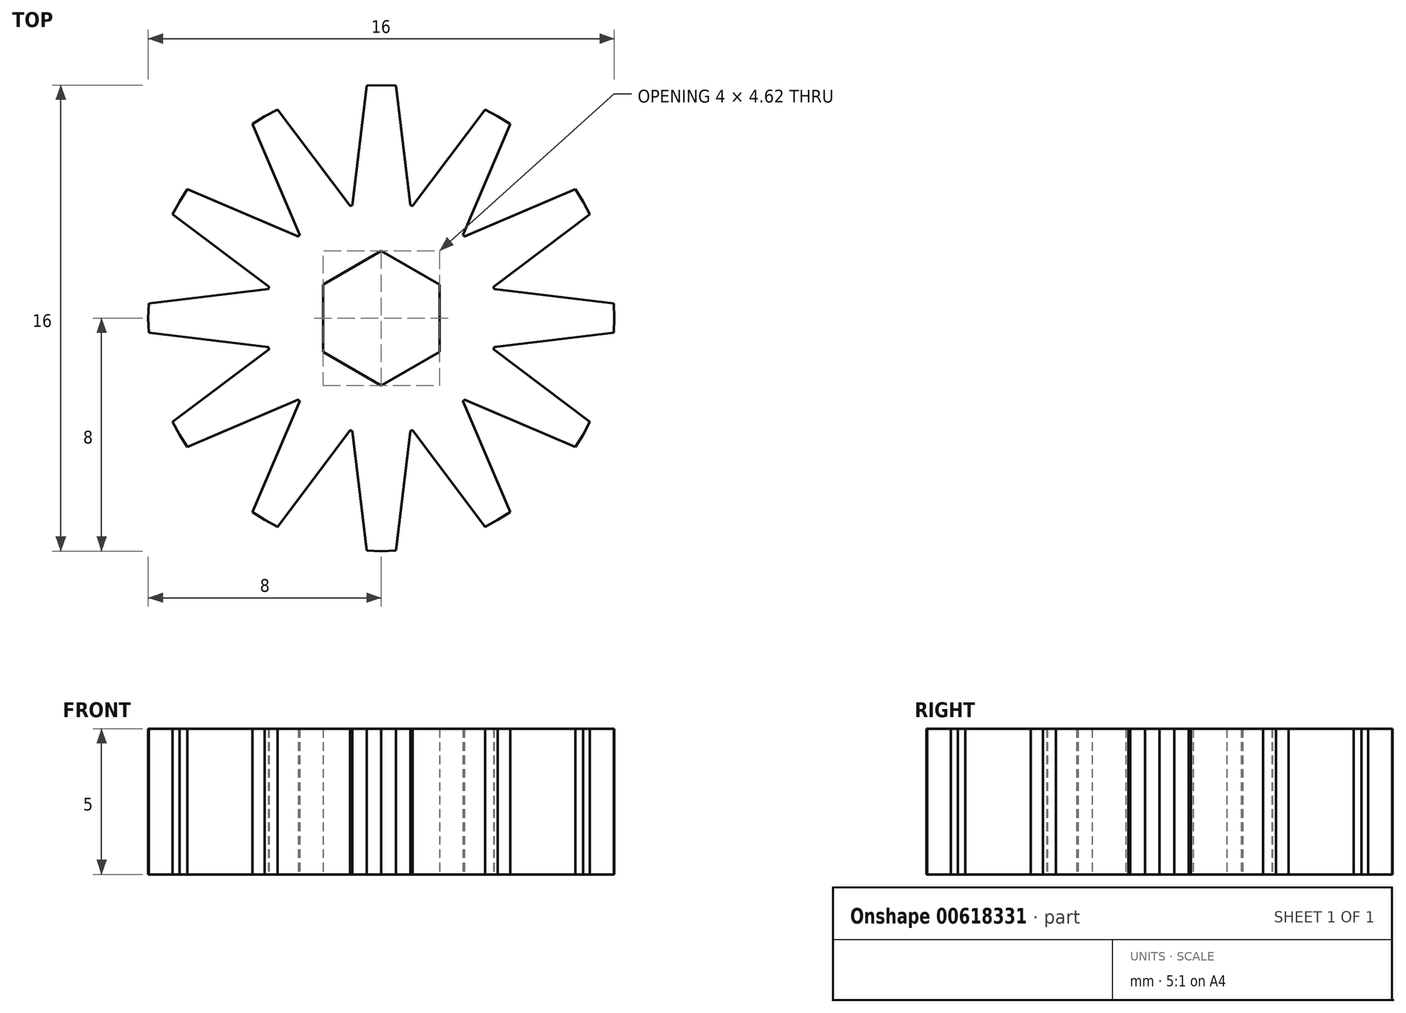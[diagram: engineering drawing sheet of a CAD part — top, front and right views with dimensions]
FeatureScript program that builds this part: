
annotation { "Feature Type Name" : "Feature", "Feature Type Description" : "" }
export const myFeature = defineFeature(function(context is Context, id is Id, definition is map)
    precondition{}
    {
        {
            var Q0;
            Q0=qCreatedBy(makeId("Top.planeOp"),FACE);
            var sketch = newSketch(context, id + "F0", { "sketchPlane" : qUnion([Q0])});
            skCircle(sketch, "E0", {"center": v(0, 0) * mm, "radius": 2 * mm});
            skCircle(sketch, "E1", {"center": v(0, 0) * mm, "radius": 8 * mm});
            skCircle(sketch, "E2.cCircle", {"center": v(0, 0) * mm, "radius": 2 * mm, "construction": true});
            skLineSegment(sketch, "E2.0", {"start": v(2, 1.15) * mm, "end": v(2, -1.15) * mm});
            skLineSegment(sketch, "E2.1", {"start": v(2, -1.15) * mm, "end": v(0, -2.3) * mm});
            skLineSegment(sketch, "E2.2", {"start": v(0, -2.3) * mm, "end": v(-2, -1.15) * mm});
            skLineSegment(sketch, "E2.3", {"start": v(-2, -1.15) * mm, "end": v(-2, 1.15) * mm});
            skLineSegment(sketch, "E2.4", {"start": v(-2, 1.15) * mm, "end": v(0, 2.3) * mm});
            skLineSegment(sketch, "E2.5", {"start": v(0, 2.3) * mm, "end": v(2, 1.15) * mm});
            skCircle(sketch, "E3", {"center": v(0, 0) * mm, "radius": 4 * mm});
            skLineSegment(sketch, "E4", {"start": v(0, 8) * mm, "end": v(-0.5, 7.98) * mm});
            skLineSegment(sketch, "E5", {"start": v(-0.5, 7.98) * mm, "end": v(-1, 3.87) * mm});
            skLineSegment(sketch, "E6.MirrorCS", {"start": v(0.5, 7.98) * mm, "end": v(1, 3.87) * mm});
            skLineSegment(sketch, "E7.MirrorCS", {"start": v(0, 8) * mm, "end": v(0.5, 7.98) * mm});
            skPoint(sketch, "E8.center", {"position": v(0, 2) * mm});
            skLineSegment(sketch, "E9.1.0", {"start": v(-4.42, 6.66) * mm, "end": v(-2.8, 2.85) * mm});
            skLineSegment(sketch, "E9.1.1", {"start": v(-4, 6.93) * mm, "end": v(-3.56, 7.16) * mm});
            skLineSegment(sketch, "E9.1.2", {"start": v(-4, 6.93) * mm, "end": v(-4.42, 6.66) * mm});
            skLineSegment(sketch, "E9.1.3", {"start": v(-3.56, 7.16) * mm, "end": v(-1.07, 3.85) * mm});
            skLineSegment(sketch, "E9.2.0", {"start": v(-7.16, 3.56) * mm, "end": v(-3.85, 1.07) * mm});
            skLineSegment(sketch, "E9.2.1", {"start": v(-6.93, 4) * mm, "end": v(-6.66, 4.42) * mm});
            skLineSegment(sketch, "E9.2.2", {"start": v(-6.93, 4) * mm, "end": v(-7.16, 3.56) * mm});
            skLineSegment(sketch, "E9.2.3", {"start": v(-6.66, 4.42) * mm, "end": v(-2.85, 2.8) * mm});
            skLineSegment(sketch, "E9.3.0", {"start": v(-7.98, -0.5) * mm, "end": v(-3.87, -1) * mm});
            skLineSegment(sketch, "E9.3.1", {"start": v(-8, 0) * mm, "end": v(-7.98, 0.5) * mm});
            skLineSegment(sketch, "E9.3.2", {"start": v(-8, 0) * mm, "end": v(-7.98, -0.5) * mm});
            skLineSegment(sketch, "E9.3.3", {"start": v(-7.98, 0.5) * mm, "end": v(-3.87, 1) * mm});
            skLineSegment(sketch, "E9.4.0", {"start": v(-6.66, -4.42) * mm, "end": v(-2.85, -2.8) * mm});
            skLineSegment(sketch, "E9.4.1", {"start": v(-6.93, -4) * mm, "end": v(-7.16, -3.56) * mm});
            skLineSegment(sketch, "E9.4.2", {"start": v(-6.93, -4) * mm, "end": v(-6.66, -4.42) * mm});
            skLineSegment(sketch, "E9.4.3", {"start": v(-7.16, -3.56) * mm, "end": v(-3.85, -1.07) * mm});
            skLineSegment(sketch, "E9.5.0", {"start": v(-3.56, -7.16) * mm, "end": v(-1.07, -3.85) * mm});
            skLineSegment(sketch, "E9.5.1", {"start": v(-4, -6.93) * mm, "end": v(-4.42, -6.66) * mm});
            skLineSegment(sketch, "E9.5.2", {"start": v(-4, -6.93) * mm, "end": v(-3.56, -7.16) * mm});
            skLineSegment(sketch, "E9.5.3", {"start": v(-4.42, -6.66) * mm, "end": v(-2.8, -2.85) * mm});
            skLineSegment(sketch, "E9.6.0", {"start": v(0.5, -7.98) * mm, "end": v(1, -3.87) * mm});
            skLineSegment(sketch, "E9.6.1", {"start": v(0, -8) * mm, "end": v(-0.5, -7.98) * mm});
            skLineSegment(sketch, "E9.6.2", {"start": v(0, -8) * mm, "end": v(0.5, -7.98) * mm});
            skLineSegment(sketch, "E9.6.3", {"start": v(-0.5, -7.98) * mm, "end": v(-1, -3.87) * mm});
            skLineSegment(sketch, "E9.7.0", {"start": v(4.42, -6.66) * mm, "end": v(2.8, -2.85) * mm});
            skLineSegment(sketch, "E9.7.1", {"start": v(4, -6.93) * mm, "end": v(3.56, -7.16) * mm});
            skLineSegment(sketch, "E9.7.2", {"start": v(4, -6.93) * mm, "end": v(4.42, -6.66) * mm});
            skLineSegment(sketch, "E9.7.3", {"start": v(3.56, -7.16) * mm, "end": v(1.07, -3.85) * mm});
            skLineSegment(sketch, "E9.8.0", {"start": v(7.16, -3.56) * mm, "end": v(3.85, -1.07) * mm});
            skLineSegment(sketch, "E9.8.1", {"start": v(6.93, -4) * mm, "end": v(6.66, -4.42) * mm});
            skLineSegment(sketch, "E9.8.2", {"start": v(6.93, -4) * mm, "end": v(7.16, -3.56) * mm});
            skLineSegment(sketch, "E9.8.3", {"start": v(6.66, -4.42) * mm, "end": v(2.85, -2.8) * mm});
            skLineSegment(sketch, "E9.9.0", {"start": v(7.98, 0.5) * mm, "end": v(3.87, 1) * mm});
            skLineSegment(sketch, "E9.9.1", {"start": v(8, 0) * mm, "end": v(7.98, -0.5) * mm});
            skLineSegment(sketch, "E9.9.2", {"start": v(8, 0) * mm, "end": v(7.98, 0.5) * mm});
            skLineSegment(sketch, "E9.9.3", {"start": v(7.98, -0.5) * mm, "end": v(3.87, -1) * mm});
            skLineSegment(sketch, "E9.10.0", {"start": v(6.66, 4.42) * mm, "end": v(2.85, 2.8) * mm});
            skLineSegment(sketch, "E9.10.1", {"start": v(6.93, 4) * mm, "end": v(7.16, 3.56) * mm});
            skLineSegment(sketch, "E9.10.2", {"start": v(6.93, 4) * mm, "end": v(6.66, 4.42) * mm});
            skLineSegment(sketch, "E9.10.3", {"start": v(7.16, 3.56) * mm, "end": v(3.85, 1.07) * mm});
            skLineSegment(sketch, "E9.11.0", {"start": v(3.56, 7.16) * mm, "end": v(1.07, 3.85) * mm});
            skLineSegment(sketch, "E9.11.1", {"start": v(4, 6.93) * mm, "end": v(4.42, 6.66) * mm});
            skLineSegment(sketch, "E9.11.2", {"start": v(4, 6.93) * mm, "end": v(3.56, 7.16) * mm});
            skLineSegment(sketch, "E9.11.3", {"start": v(4.42, 6.66) * mm, "end": v(2.8, 2.85) * mm});
            skSolve(sketch);
        }
        {
            var Q0;
            Q0=makeQuery(id+"F0.imprint","IMPRINT",FACE,{"disambiguationData":[TD([[makeQuery(id+"F0.imprint","IMPRINT",EDGE,{"derivedFrom":sQuery(id+"F0.wireOp",EDGE,"E4")}),1.0]])]});
            var Q1;
            Q1=makeQuery(id+"F0.imprint","IMPRINT",FACE,{"disambiguationData":[TD([[makeQuery(id+"F0.imprint","IMPRINT",EDGE,{"derivedFrom":sQuery(id+"F0.wireOp",EDGE,"E8.1.0")}),1.0]])]});
            var Q2;
            Q2=makeQuery(id+"F0.imprint","IMPRINT",FACE,{"disambiguationData":[TD([[makeQuery(id+"F0.imprint","IMPRINT",EDGE,{"derivedFrom":sQuery(id+"F0.wireOp",EDGE,"E8.2.0")}),1.0]])]});
            var Q3;
            Q3=makeQuery(id+"F0.imprint","IMPRINT",FACE,{"disambiguationData":[TD([[makeQuery(id+"F0.imprint","IMPRINT",EDGE,{"derivedFrom":sQuery(id+"F0.wireOp",EDGE,"E8.3.0")}),1.0]])]});
            var Q4;
            Q4=makeQuery(id+"F0.imprint","IMPRINT",FACE,{"disambiguationData":[TD([[makeQuery(id+"F0.imprint","IMPRINT",EDGE,{"derivedFrom":sQuery(id+"F0.wireOp",EDGE,"E8.4.0")}),1.0]])]});
            var Q5;
            Q5=makeQuery(id+"F0.imprint","IMPRINT",FACE,{"disambiguationData":[TD([[makeQuery(id+"F0.imprint","IMPRINT",EDGE,{"derivedFrom":sQuery(id+"F0.wireOp",EDGE,"E8.5.0")}),1.0]])]});
            var Q6;
            Q6=makeQuery(id+"F0.imprint","IMPRINT",FACE,{"disambiguationData":[TD([[makeQuery(id+"F0.imprint","IMPRINT",EDGE,{"derivedFrom":sQuery(id+"F0.wireOp",EDGE,"E8.6.0")}),1.0]])]});
            var Q7;
            Q7=makeQuery(id+"F0.imprint","IMPRINT",FACE,{"disambiguationData":[TD([[makeQuery(id+"F0.imprint","IMPRINT",EDGE,{"derivedFrom":sQuery(id+"F0.wireOp",EDGE,"E8.7.0")}),1.0]])]});
            var Q8;
            Q8=makeQuery(id+"F0.imprint","IMPRINT",FACE,{"disambiguationData":[TD([[makeQuery(id+"F0.imprint","IMPRINT",EDGE,{"derivedFrom":sQuery(id+"F0.wireOp",EDGE,"E8.8.0")}),1.0]])]});
            var Q9;
            Q9=makeQuery(id+"F0.imprint","IMPRINT",FACE,{"disambiguationData":[TD([[makeQuery(id+"F0.imprint","IMPRINT",EDGE,{"derivedFrom":sQuery(id+"F0.wireOp",EDGE,"E8.9.0")}),1.0]])]});
            var Q10;
            Q10=makeQuery(id+"F0.imprint","IMPRINT",FACE,{"disambiguationData":[TD([[makeQuery(id+"F0.imprint","IMPRINT",EDGE,{"derivedFrom":sQuery(id+"F0.wireOp",EDGE,"E8.10.0")}),1.0]])]});
            var Q11;
            Q11=makeQuery(id+"F0.imprint","IMPRINT",FACE,{"disambiguationData":[TD([[makeQuery(id+"F0.imprint","IMPRINT",EDGE,{"derivedFrom":sQuery(id+"F0.wireOp",EDGE,"E8.11.0")}),1.0]])]});
            var Q12;
            {var subQ12=sQuery(id+"F0.wireOp",EDGE,"E2.5");var subQ13=sQuery(id+"F0.wireOp",EDGE,"E2.0");var subQ14=makeQuery(id+"F0.imprint","INTERSECT",VERTEX,{"derivedFrom":[subQ13,subQ12]});Q12=makeQuery(id+"F0.imprint","IMPRINT",FACE,{"disambiguationData":[TD([[makeQuery(id+"F0.imprint","IMPRINT",EDGE,{"disambiguationData":[TD([[subQ14,-1.0]])],"derivedFrom":subQ13}),1.0]])]});}
            var Q13;
            {var subQ0=sQuery(id+"F0.wireOp",EDGE,"E9.11.0");Q13=makeQuery(id+"F0.imprint","IMPRINT",FACE,{"disambiguationData":[TD([[makeQuery(id+"F0.imprint","IMPRINT",EDGE,{"derivedFrom":subQ0}),1.0]])]});}
            var Q14;
            {var subQ0=sQuery(id+"F0.wireOp",EDGE,"E9.10.0");Q14=makeQuery(id+"F0.imprint","IMPRINT",FACE,{"disambiguationData":[TD([[makeQuery(id+"F0.imprint","IMPRINT",EDGE,{"derivedFrom":subQ0}),1.0]])]});}
            var Q15;
            {var subQ0=sQuery(id+"F0.wireOp",EDGE,"E9.9.0");Q15=makeQuery(id+"F0.imprint","IMPRINT",FACE,{"disambiguationData":[TD([[makeQuery(id+"F0.imprint","IMPRINT",EDGE,{"derivedFrom":subQ0}),1.0]])]});}
            var Q16;
            {var subQ0=sQuery(id+"F0.wireOp",EDGE,"E9.8.0");Q16=makeQuery(id+"F0.imprint","IMPRINT",FACE,{"disambiguationData":[TD([[makeQuery(id+"F0.imprint","IMPRINT",EDGE,{"derivedFrom":subQ0}),1.0]])]});}
            var Q17;
            {var subQ0=sQuery(id+"F0.wireOp",EDGE,"E9.7.0");Q17=makeQuery(id+"F0.imprint","IMPRINT",FACE,{"disambiguationData":[TD([[makeQuery(id+"F0.imprint","IMPRINT",EDGE,{"derivedFrom":subQ0}),1.0]])]});}
            var Q18;
            {var subQ0=sQuery(id+"F0.wireOp",EDGE,"E9.6.0");Q18=makeQuery(id+"F0.imprint","IMPRINT",FACE,{"disambiguationData":[TD([[makeQuery(id+"F0.imprint","IMPRINT",EDGE,{"derivedFrom":subQ0}),1.0]])]});}
            var Q19;
            {var subQ0=sQuery(id+"F0.wireOp",EDGE,"E9.5.0");Q19=makeQuery(id+"F0.imprint","IMPRINT",FACE,{"disambiguationData":[TD([[makeQuery(id+"F0.imprint","IMPRINT",EDGE,{"derivedFrom":subQ0}),1.0]])]});}
            var Q20;
            {var subQ0=sQuery(id+"F0.wireOp",EDGE,"E9.4.0");Q20=makeQuery(id+"F0.imprint","IMPRINT",FACE,{"disambiguationData":[TD([[makeQuery(id+"F0.imprint","IMPRINT",EDGE,{"derivedFrom":subQ0}),1.0]])]});}
            var Q21;
            {var subQ0=sQuery(id+"F0.wireOp",EDGE,"E9.3.0");Q21=makeQuery(id+"F0.imprint","IMPRINT",FACE,{"disambiguationData":[TD([[makeQuery(id+"F0.imprint","IMPRINT",EDGE,{"derivedFrom":subQ0}),1.0]])]});}
            var Q22;
            {var subQ0=sQuery(id+"F0.wireOp",EDGE,"E9.2.0");Q22=makeQuery(id+"F0.imprint","IMPRINT",FACE,{"disambiguationData":[TD([[makeQuery(id+"F0.imprint","IMPRINT",EDGE,{"derivedFrom":subQ0}),1.0]])]});}
            var Q23;
            {var subQ0=sQuery(id+"F0.wireOp",EDGE,"E9.1.0");Q23=makeQuery(id+"F0.imprint","IMPRINT",FACE,{"disambiguationData":[TD([[makeQuery(id+"F0.imprint","IMPRINT",EDGE,{"derivedFrom":subQ0}),1.0]])]});}
            extrude(context, id + "F1", {"entities" : qUnion([Q0, Q1, Q2, Q3, Q4, Q5, Q6, Q7, Q8, Q9, Q10, Q11, Q12, Q13, Q14, Q15, Q16, Q17, Q18, Q19, Q20, Q21, Q22, Q23]), "depth" : 5 * mm, "offsetDistance" : 25 * mm});
        }
    });
